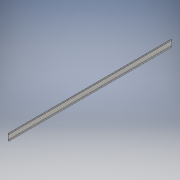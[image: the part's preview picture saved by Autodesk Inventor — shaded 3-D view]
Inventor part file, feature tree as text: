
AUTODESK INVENTOR PART (.ipt)
format: ipt  version: 2018 (Build 220112000, 112)  size: 123,392 bytes
history: native  units: mm
features: extrude x1, sketch x1
ambient origin geometry x8: Origin, YZ Plane, XZ Plane, XY Plane, X Axis, Y Axis, Z Axis, Center Point
bodies: Volumenkörper1 (feature_tree)
feature tree (2):
  extrude  "Extrusion1"  Depth=13.0mm
  sketch  "Skizze1"  dims[d0=1.15mm d1=13.0mm d2=0.3mm d3=0.3mm d4=9.3mm d7=75.0deg d8=0.3mm d9=0.3mm d10=75.0deg d11=0.3mm d12=0.3mm d13=300.0mm d14=0.0mm]
